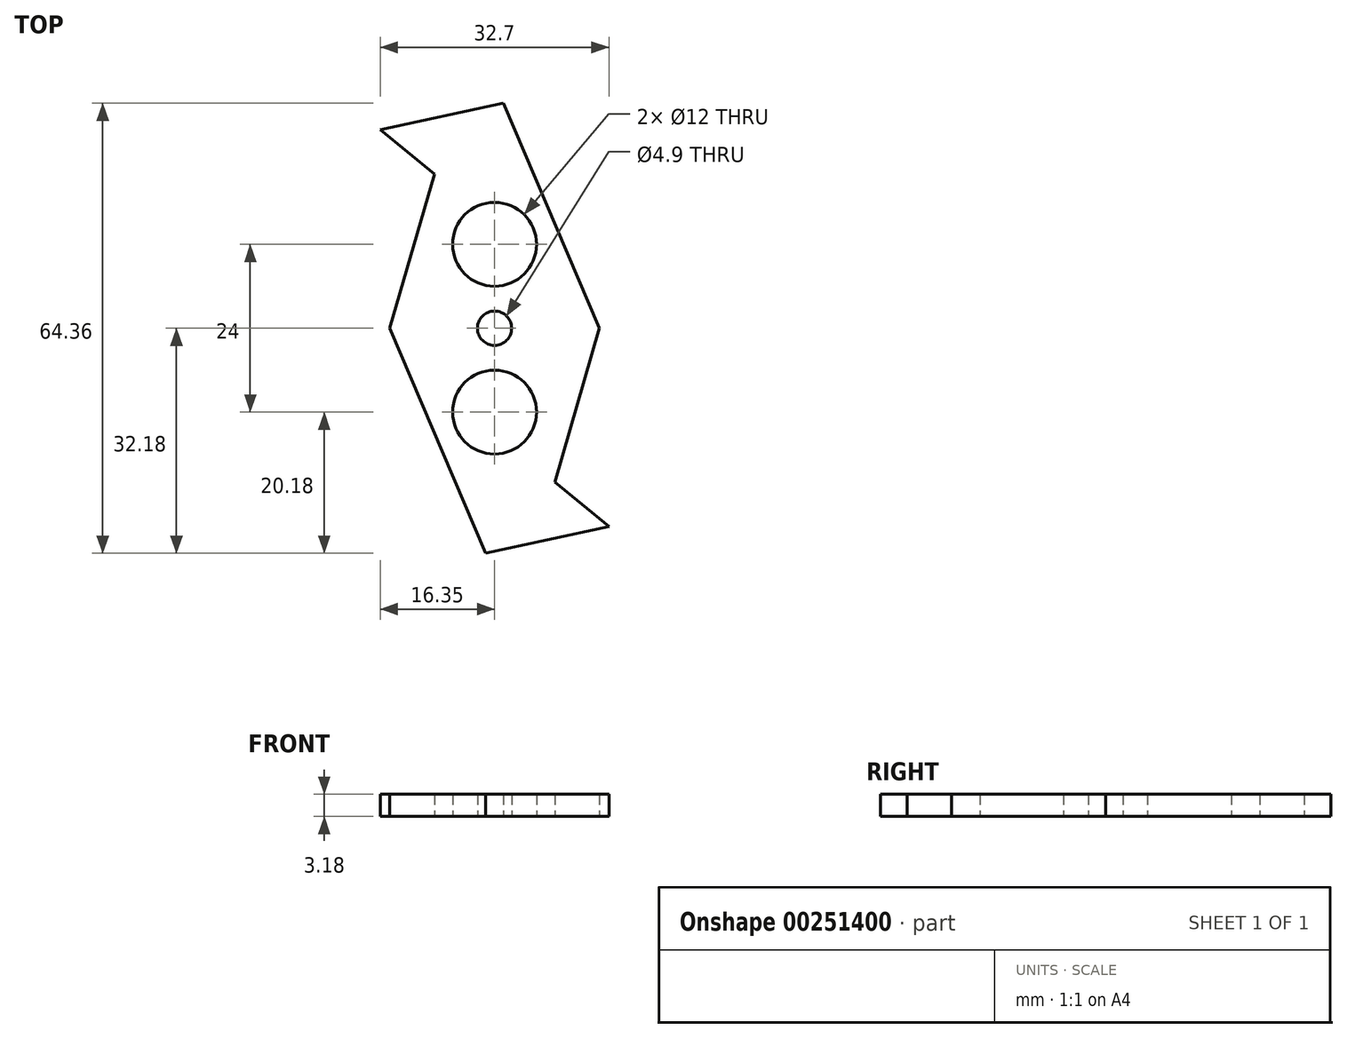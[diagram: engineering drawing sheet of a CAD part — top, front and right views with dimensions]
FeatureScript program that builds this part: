
annotation { "Feature Type Name" : "Feature", "Feature Type Description" : "" }
export const myFeature = defineFeature(function(context is Context, id is Id, definition is map)
    precondition{}
    {
        {
            var Q0;
            Q0=qCreatedBy(makeId("Top.planeOp"),FACE);
            var sketch = newSketch(context, id + "F0", { "sketchPlane" : qUnion([Q0])});
            skLineSegment(sketch, "E0.bottom", {"start": v(35, 35) * mm, "end": v(-35, 35) * mm, "construction": true});
            skLineSegment(sketch, "E0.top", {"start": v(35, -35) * mm, "end": v(-35, -35) * mm, "construction": true});
            skLineSegment(sketch, "E0.left", {"start": v(35, 35) * mm, "end": v(35, -35) * mm, "construction": true});
            skLineSegment(sketch, "E0.right", {"start": v(-35, 35) * mm, "end": v(-35, -35) * mm, "construction": true});
            skPoint(sketch, "E0.middle", {"position": v(0, 0) * mm});
            skLineSegment(sketch, "E1", {"start": v(15, 0) * mm, "end": v(1.25, 32.18) * mm});
            skLineSegment(sketch, "E2", {"start": v(1.25, 32.18) * mm, "end": v(-16.35, 28.38) * mm});
            skLineSegment(sketch, "E3", {"start": v(-16.35, 28.38) * mm, "end": v(-8.6, 22.05) * mm});
            skLineSegment(sketch, "E4", {"start": v(-8.6, 22.05) * mm, "end": v(-15, 0) * mm});
            skLineSegment(sketch, "E5.1.1", {"start": v(-1.25, -32.18) * mm, "end": v(16.35, -28.38) * mm});
            skLineSegment(sketch, "E5.1.2", {"start": v(16.35, -28.38) * mm, "end": v(8.6, -22.05) * mm});
            skLineSegment(sketch, "E5.1.3", {"start": v(-15, 0) * mm, "end": v(-1.25, -32.18) * mm});
            skLineSegment(sketch, "E5.1.4", {"start": v(8.6, -22.05) * mm, "end": v(15, 0) * mm});
            skCircle(sketch, "E6", {"center": v(0, 0) * mm, "radius": 2.45 * mm});
            skCircle(sketch, "E7", {"center": v(0, 12) * mm, "radius": 6 * mm});
            skCircle(sketch, "E8.MirrorC", {"center": v(0, -12) * mm, "radius": 6 * mm});
            skSolve(sketch);
        }
        {
            var Q0;
            Q0=makeQuery(id+"F0.imprint","IMPRINT",FACE,{"disambiguationData":[TD([[makeQuery(id+"F0.imprint","IMPRINT",EDGE,{"derivedFrom":sQuery(id+"F0.wireOp",EDGE,"E1")}),1.0]])]});
            extrude(context, id + "F1", {"entities" : qUnion([Q0]), "depth" : 3.17 * mm, "symmetric" : true});
        }
    });
